FCSTD DOCUMENT  (FreeCAD 1.1R40971 (Git))
Label: neje-max-4
License: All rights reserved
LicenseURL: http://en.wikipedia.org/wiki/All_rights_reserved
objects: App::Link×5, App::DocumentObjectGroup×3, PartDesign::CoordinateSystem×1, App::FeaturePython×1, App::Part×1, App::Point×1
note: 1 computed .brp shape members not serialized (recipe doc carries the construction recipe); baked Part::Feature solids carry a one-line shape summary decoded from their .brp
EXTERNAL_REF file=x-frame.FCStd obj=Body
EXTERNAL_REF file=y-extrusion.FCStd obj=Body
EXTERNAL_REF file=x-rail-assy.FCStd obj=Part

FEATURE [App::DocumentObjectGroup] Parts
FEATURE [PartDesign::CoordinateSystem] LCS_Origin
  AttacherType = Attacher::AttachEngine3D
  AttachmentSupport = -> [X_Axis]
  MapMode = 2
FEATURE [App::DocumentObjectGroup] Constraints
FEATURE [App::FeaturePython] Variables  # WARN: FeaturePython — macro-defined, semantics opaque (R4)
  Type = App::PropertyContainer
FEATURE [App::DocumentObjectGroup] Configurations
FEATURE [App::Link] Body  label="rail-back"
  LinkPlacement = pos=(-2.5736e-05,294.386,0) rot=(0,0,1;3.14159rad)
  LinkedObject = -> <external x-frame.FCStd>#Body
  Placement = pos=(-2.5736e-05,294.386,0) rot=(0,0,1;3.14159rad)
FEATURE [App::Link] rail_back  label="rail-front"
  LinkPlacement = pos=(0,-294.386,0) rot=(0,0,1;0rad)
  LinkedObject = -> <external x-frame.FCStd>#Body
  Placement = pos=(0,-294.386,0) rot=(0,0,1;0rad)
FEATURE [App::Link] Body001  label="rail-left"
  LinkPlacement = pos=(-439.723,4.89331e-05,29.242) rot=(0,0,1;0rad)
  LinkedObject = -> <external y-extrusion.FCStd>#Body
  Placement = pos=(-439.723,4.89331e-05,29.242) rot=(0,0,1;0rad)
FEATURE [App::Link] Body002  label="rail-right"
  LinkPlacement = pos=(439.926,-5.59382e-05,29.3182) rot=(0,0,1;0rad)
  LinkedObject = -> <external y-extrusion.FCStd>#Body
  Placement = pos=(439.926,-5.59382e-05,29.3182) rot=(0,0,1;0rad)
FEATURE [App::Link] Part  label="x-rail"
  LinkPlacement = pos=(0,0,45.72) rot=(0,0,1;0rad)
  LinkedObject = -> <external x-rail-assy.FCStd>#Part
  Placement = pos=(0,0,45.72) rot=(0,0,1;0rad)
FEATURE [App::Part] Assembly
  AssemblyType = Part::Link
  Group = -> [LCS_Origin,Constraints,Variables,Configurations,Body,rail_back,Body001,Body002,Part]
  Origin = -> Origin
  Type = Assembly
FEATURE [App::Point] Origin001  label="Origin"
  Role = Origin

RESOLVED EXTERNAL PARTS (link-assembly join: the EXTERNAL_REF files above that resolve inside this repo's crawl, each included once):
---- part x-frame.FCStd = doc fcstd_80ce30af8bc4 ----
FCSTD DOCUMENT  (FreeCAD 1.1R40971 (Git))
Label: x-frame
License: All rights reserved
LicenseURL: http://en.wikipedia.org/wiki/All_rights_reserved
objects: Sketcher::SketchObject×4, PartDesign::Pocket×2, PartDesign::Pad×1, PartDesign::Hole×1, PartDesign::Body×1, App::Point×1
note: 21 computed .brp shape members not serialized (recipe doc carries the construction recipe); baked Part::Feature solids carry a one-line shape summary decoded from their .brp

FEATURE [Sketcher::SketchObject] Sketch
  ArcFitTolerance = 0
  ExternalTypes = [0]
  FullyConstrained = true
  MakeInternals = false
  Placement = pos=(0,0,0) rot=(0.57735,0.57735,0.57735;2.0944rad)
  sketch-geometry (6):
    g0: LineSegment StartX=0 StartY=60 StartZ=0 EndX=4.7 EndY=60 EndZ=0
    g1: LineSegment StartX=26 StartY=4.7 StartZ=0 EndX=26 EndY=0 EndZ=0
    g2: LineSegment StartX=26 StartY=0 StartZ=0 EndX=0 EndY=0 EndZ=0
    g3: LineSegment StartX=0 StartY=0 StartZ=0 EndX=0 EndY=60 EndZ=0
    g4: LineSegment StartX=26 StartY=4.7 StartZ=0 EndX=4.7 EndY=4.7 EndZ=0
    g5: LineSegment StartX=4.7 StartY=4.7 StartZ=0 EndX=4.7 EndY=60 EndZ=0
  constraints (17):
    c: Coincident(g1,g2)
    c: Coincident(g2,g3)
    c: Coincident(g3,g0)
    c: Horizontal(g0)
    c: Horizontal(g2)
    c: Vertical(g1)
    c: Vertical(g3)
    c: Coincident(g4,g5)
    c: Horizontal(g4)
    c: Vertical(g5)
    c: Coincident(g5,g0)
    c: Coincident(g4,g1)
    c: Equal(g1,g0)
    c: DistanceY(g1,g1) = 4.7
    c: DistanceX(g2,g2) = 26
    c: DistanceY(g3,g3) = 60
    c: Coincident(g2,g-1)
FEATURE [PartDesign::Pad] Pad
  Direction = (1,1e-16,-1e-16)
  Length = 920
  Length2 = 10
  Midplane = true
  Placement = pos=(0,0,0) rot=(0.57735,0.57735,0.57735;2.0944rad)
  Profile = -> Sketch
  ReferenceAxis = -> Sketch [N_Axis]
  Suppressed = false
  Type = 0
FEATURE [Sketcher::SketchObject] Sketch001
  ArcFitTolerance = 0
  AttachmentSupport = -> [Pad]
  ExternalTypes = [0]
  FullyConstrained = true
  MakeInternals = false
  MapMode = 5
  Placement = pos=(0,0,0) rot=(0.57735,0.57735,-0.57735;2.0944rad)
  sketch-geometry (8):
    g0: LineSegment StartX=-70 StartY=-427.5 StartZ=0 EndX=-36 EndY=-427.5 EndZ=0
    g1: LineSegment StartX=-30 StartY=-421.5 StartZ=0 EndX=-30 EndY=421.5 EndZ=0
    g2: LineSegment StartX=-36 StartY=427.5 StartZ=0 EndX=-70 EndY=427.5 EndZ=0
    g3: LineSegment StartX=-70 StartY=427.5 StartZ=0 EndX=-70 EndY=-427.5 EndZ=0
    g4: ArcOfCircle CenterX=-36 CenterY=-421.5 CenterZ=0 NormalX=0 NormalY=0 NormalZ=1 AngleXU=0 Radius=6 StartAngle=4.71239 EndAngle=6.28319
    g5: GeomPoint [constr] X=-30 Y=-427.5 Z=0
    g6: ArcOfCircle CenterX=-36 CenterY=421.5 CenterZ=0 NormalX=0 NormalY=0 NormalZ=1 AngleXU=0 Radius=6 StartAngle=-8.9e-13 EndAngle=1.5708
    g7: GeomPoint [constr] X=-30 Y=427.5 Z=0
  constraints (19):
    c: Coincident(g2,g3)
    c: Coincident(g3,g0)
    c: Horizontal(g0)
    c: Horizontal(g2)
    c: Vertical(g1)
    c: DistanceX(g7,g-1) = 30
    c: PointOnObject(g5,g0)
    c: PointOnObject(g5,g1)
    c: Tangent(g0,g4) = -1.5708
    c: Tangent(g1,g4) = -1.5708
    c: PointOnObject(g7,g1)
    c: PointOnObject(g7,g2)
    c: Tangent(g1,g6) = -1.5708
    c: Tangent(g2,g6) = -1.5708
    c: Equal(g6,g4)
    c: Diameter(g4) = 12
    c: DistanceX(g0,g-1) = 70
    c: Symmetric(g2,g0,g-1)
    c: DistanceY(g3,g3) = 855
FEATURE [PartDesign::Pocket] Pocket
  BaseFeature = -> Pad
  Direction = (0,1,0)
  Length = 5
  Length2 = 5
  Midplane = true
  Placement = pos=(0,0,0) rot=(0.57735,0.57735,0.57735;2.0944rad)
  Profile = -> Sketch001
  ReferenceAxis = -> Sketch001 [N_Axis]
  Suppressed = false
  Type = 1
FEATURE [Sketcher::SketchObject] Sketch002
  ArcFitTolerance = 0
  AttachmentSupport = -> [Pocket]
  ExternalTypes = [0]
  FullyConstrained = true
  MakeInternals = false
  MapMode = 5
  Placement = pos=(2.1e-15,-2.6e-15,4.7) rot=(0,0,-1;1.5708rad)
  sketch-geometry (41):
    g0: Circle CenterX=-14.7 CenterY=455 CenterZ=0 NormalX=0 NormalY=0 NormalZ=1 AngleXU=0 Radius=2.5
    g1: Circle CenterX=-14.7 CenterY=409.5 CenterZ=0 NormalX=0 NormalY=0 NormalZ=1 AngleXU=0 Radius=2.5
    g2: LineSegment [constr] StartX=-14.7 StartY=455 StartZ=0 EndX=-14.7 EndY=409.5 EndZ=0
    g3: Circle CenterX=-14.7 CenterY=364 CenterZ=0 NormalX=0 NormalY=0 NormalZ=1 AngleXU=0 Radius=2.5
    g4: LineSegment [constr] StartX=-14.7 StartY=409.5 StartZ=0 EndX=-14.7 EndY=364 EndZ=0
    g5: Circle CenterX=-14.7 CenterY=318.5 CenterZ=0 NormalX=0 NormalY=0 NormalZ=1 AngleXU=0 Radius=2.5
    g6: LineSegment [constr] StartX=-14.7 StartY=364 StartZ=0 EndX=-14.7 EndY=318.5 EndZ=0
    g7: Circle CenterX=-14.7 CenterY=273 CenterZ=0 NormalX=0 NormalY=0 NormalZ=1 AngleXU=0 Radius=2.5
    g8: LineSegment [constr] StartX=-14.7 StartY=318.5 StartZ=0 EndX=-14.7 EndY=273 EndZ=0
    g9: Circle CenterX=-14.7 CenterY=227.5 CenterZ=0 NormalX=0 NormalY=0 NormalZ=1 AngleXU=0 Radius=2.5
    g10: LineSegment [constr] StartX=-14.7 StartY=273 StartZ=0 EndX=-14.7 EndY=227.5 EndZ=0
    g11: Circle CenterX=-14.7 CenterY=182 CenterZ=0 NormalX=0 NormalY=0 NormalZ=1 AngleXU=0 Radius=2.5
    g12: LineSegment [constr] StartX=-14.7 StartY=227.5 StartZ=0 EndX=-14.7 EndY=182 EndZ=0
    g13: Circle CenterX=-14.7 CenterY=136.5 CenterZ=0 NormalX=0 NormalY=0 NormalZ=1 AngleXU=0 Radius=2.5
    g14: LineSegment [constr] StartX=-14.7 StartY=182 StartZ=0 EndX=-14.7 EndY=136.5 EndZ=0
    g15: Circle CenterX=-14.7 CenterY=91 CenterZ=0 NormalX=0 NormalY=0 NormalZ=1 AngleXU=0 Radius=2.5
    g16: LineSegment [constr] StartX=-14.7 StartY=136.5 StartZ=0 EndX=-14.7 EndY=91 EndZ=0
    g17: Circle CenterX=-14.7 CenterY=45.5 CenterZ=0 NormalX=0 NormalY=0 NormalZ=1 AngleXU=0 Radius=2.5
    g18: LineSegment [constr] StartX=-14.7 StartY=91 StartZ=0 EndX=-14.7 EndY=45.5 EndZ=0
    g19: Circle CenterX=-14.7 CenterY=0 CenterZ=0 NormalX=0 NormalY=0 NormalZ=1 AngleXU=0 Radius=2.5
    g20: LineSegment [constr] StartX=-14.7 StartY=45.5 StartZ=0 EndX=-14.7 EndY=0 EndZ=0
    g21: Circle CenterX=-14.7 CenterY=-45.5 CenterZ=0 NormalX=0 NormalY=0 NormalZ=1 AngleXU=0 Radius=2.5
    g22: LineSegment [constr] StartX=-14.7 StartY=0 StartZ=0 EndX=-14.7 EndY=-45.5 EndZ=0
    g23: Circle CenterX=-14.7 CenterY=-91 CenterZ=0 NormalX=0 NormalY=0 NormalZ=1 AngleXU=0 Radius=2.5
    g24: LineSegment [constr] StartX=-14.7 StartY=-45.5 StartZ=0 EndX=-14.7 EndY=-91 EndZ=0
    g25: Circle CenterX=-14.7 CenterY=-136.5 CenterZ=0 NormalX=0 NormalY=0 NormalZ=1 AngleXU=0 Radius=2.5
    g26: LineSegment [constr] StartX=-14.7 StartY=-91 StartZ=0 EndX=-14.7 EndY=-136.5 EndZ=0
    g27: Circle CenterX=-14.7 CenterY=-182 CenterZ=0 NormalX=0 NormalY=0 NormalZ=1 AngleXU=0 Radius=2.5
    g28: LineSegment [constr] StartX=-14.7 StartY=-136.5 StartZ=0 EndX=-14.7 EndY=-182 EndZ=0
    g29: Circle CenterX=-14.7 CenterY=-227.5 CenterZ=0 NormalX=0 NormalY=0 NormalZ=1 AngleXU=0 Radius=2.5
    g30: LineSegment [constr] StartX=-14.7 StartY=-182 StartZ=0 EndX=-14.7 EndY=-227.5 EndZ=0
    g31: Circle CenterX=-14.7 CenterY=-273 CenterZ=0 NormalX=0 NormalY=0 NormalZ=1 AngleXU=0 Radius=2.5
    g32: LineSegment [constr] StartX=-14.7 StartY=-227.5 StartZ=0 EndX=-14.7 EndY=-273 EndZ=0
    g33: Circle CenterX=-14.7 CenterY=-318.5 CenterZ=0 NormalX=0 NormalY=0 NormalZ=1 AngleXU=0 Radius=2.5
    g34: LineSegment [constr] StartX=-14.7 StartY=-273 StartZ=0 EndX=-14.7 EndY=-318.5 EndZ=0
    g35: Circle CenterX=-14.7 CenterY=-364 CenterZ=0 NormalX=0 NormalY=0 NormalZ=1 AngleXU=0 Radius=2.5
    g36: LineSegment [constr] StartX=-14.7 StartY=-318.5 StartZ=0 EndX=-14.7 EndY=-364 EndZ=0
    g37: Circle CenterX=-14.7 CenterY=-409.5 CenterZ=0 NormalX=0 NormalY=0 NormalZ=1 AngleXU=0 Radius=2.5
    g38: LineSegment [constr] StartX=-14.7 StartY=-364 StartZ=0 EndX=-14.7 EndY=-409.5 EndZ=0
    g39: Circle CenterX=-14.7 CenterY=-455 CenterZ=0 NormalX=0 NormalY=0 NormalZ=1 AngleXU=0 Radius=2.5
    g40: LineSegment [constr] StartX=-14.7 StartY=-409.5 StartZ=0 EndX=-14.7 EndY=-455 EndZ=0
  constraints (102):
    c: Diameter(g0) = 5
    c: Equal(g0,g1) = 5
    c: Coincident(g0,g2)
    c: Coincident(g1,g2)
    c: Distance(g2) = 45.5
    c: Equal(g0,g3) = 5
    c: Coincident(g1,g4)
    c: Coincident(g3,g4)
    c: Equal(g2,g4)
    c: Parallel(g4,g2)
    c: Equal(g0,g5) = 5
    c: Coincident(g3,g6)
    c: Coincident(g5,g6)
    c: Equal(g2,g6)
    c: Parallel(g6,g2)
    c: Equal(g0,g7) = 5
    c: Coincident(g5,g8)
    c: Coincident(g7,g8)
    c: Equal(g2,g8)
    c: Parallel(g8,g2)
    c: Equal(g0,g9) = 5
    c: Coincident(g7,g10)
    c: Coincident(g9,g10)
    c: Equal(g2,g10)
    c: Parallel(g10,g2)
    c: Equal(g0,g11) = 5
    c: Coincident(g9,g12)
    c: Coincident(g11,g12)
    c: Equal(g2,g12)
    c: Parallel(g12,g2)
    c: Equal(g0,g13) = 5
    c: Coincident(g11,g14)
    c: Coincident(g13,g14)
    c: Equal(g2,g14)
    c: Parallel(g14,g2)
    c: Equal(g0,g15) = 5
    c: Coincident(g13,g16)
    c: Coincident(g15,g16)
    c: Equal(g2,g16)
    c: Parallel(g16,g2)
    c: Equal(g0,g17) = 5
    c: Coincident(g15,g18)
    c: Coincident(g17,g18)
    c: Equal(g2,g18)
    c: Parallel(g18,g2)
    c: Equal(g0,g19) = 5
    c: Coincident(g17,g20)
    c: Coincident(g19,g20)
    c: Equal(g2,g20)
    c: Parallel(g20,g2)
    c: Equal(g0,g21) = 5
    c: Coincident(g19,g22)
    c: Coincident(g21,g22)
    c: Equal(g2,g22)
    c: Parallel(g22,g2)
    c: Equal(g0,g23) = 5
    c: Coincident(g21,g24)
    c: Coincident(g23,g24)
    c: Equal(g2,g24)
    c: Parallel(g24,g2)
    c: Equal(g0,g25) = 5
    c: Coincident(g23,g26)
    c: Coincident(g25,g26)
    c: Equal(g2,g26)
    c: Parallel(g26,g2)
    c: Equal(g0,g27) = 5
    c: Coincident(g25,g28)
    c: Coincident(g27,g28)
    c: Equal(g2,g28)
    c: Parallel(g28,g2)
    c: Equal(g0,g29) = 5
    c: Coincident(g27,g30)
    c: Coincident(g29,g30)
    c: Equal(g2,g30)
    c: Parallel(g30,g2)
    c: Equal(g0,g31) = 5
    c: Coincident(g29,g32)
    c: Coincident(g31,g32)
    c: Equal(g2,g32)
    c: Parallel(g32,g2)
    c: Equal(g0,g33) = 5
    c: Coincident(g31,g34)
    c: Coincident(g33,g34)
    c: Equal(g2,g34)
    c: Parallel(g34,g2)
    c: Equal(g0,g35) = 5
    c: Coincident(g33,g36)
    c: Coincident(g35,g36)
    c: Equal(g2,g36)
    c: Parallel(g36,g2)
    c: Equal(g0,g37) = 5
    c: Coincident(g35,g38)
    c: Coincident(g37,g38)
    c: Equal(g2,g38)
    c: Parallel(g38,g2)
    c: Equal(g0,g39) = 5
    c: Coincident(g37,g40)
    c: Coincident(g39,g40)
    c: Equal(g2,g40)
    c: Parallel(g40,g2)
    c: DistanceX(g39,g-1) = 14.7
    c: Symmetric(g39,g0,g-1)
FEATURE [PartDesign::Hole] Hole
  BaseFeature = -> Pocket
  CustomThreadClearance = 0
  Depth = 25
  DepthType = 0
  Diameter = 6
  DrillForDepth = false
  DrillPoint = 1
  DrillPointAngle = 118
  HoleCutCountersinkAngle = 90
  HoleCutCustomValues = false
  HoleCutDepth = 0
  HoleCutDiameter = 6.1
  HoleCutType = 0
  ModelThread = false
  Placement = pos=(0,0,0) rot=(0.57735,0.57735,0.57735;2.0944rad)
  Profile = -> Sketch002
  Suppressed = false
  Tapered = false
  TaperedAngle = 90
  ThreadClass = 0
  ThreadDepth = 25
  ThreadDepthType = 0
  ThreadDiameter = 6
  ThreadDirection = 0
  ThreadFit = 0
  ThreadSize = 0
  ThreadType = 0
  Threaded = false
  UseCustomThreadClearance = false
FEATURE [Sketcher::SketchObject] Sketch003
  ArcFitTolerance = 0
  AttachmentSupport = -> [Hole]
  ExternalTypes = [0]
  FullyConstrained = true
  MakeInternals = false
  MapMode = 5
  Placement = pos=(-5.7e-15,4.7,3.7e-15) rot=(-0.57735,-0.57735,-0.57735;2.0944rad)
  sketch-geometry (18):
    g0: Circle CenterX=37.3 CenterY=-440 CenterZ=0 NormalX=0 NormalY=0 NormalZ=1 AngleXU=0 Radius=3.25
    g1: Circle CenterX=51.3 CenterY=-440 CenterZ=0 NormalX=0 NormalY=0 NormalZ=1 AngleXU=0 Radius=3.25
    g2: ArcOfCircle CenterX=56 CenterY=-437.75 CenterZ=0 NormalX=0 NormalY=0 NormalZ=1 AngleXU=0 Radius=1 StartAngle=2.4027e-12 EndAngle=3.14159
    g3: ArcOfCircle CenterX=56 CenterY=-442.25 CenterZ=0 NormalX=0 NormalY=0 NormalZ=1 AngleXU=0 Radius=1 StartAngle=3.14159 EndAngle=6.28319
    g4: LineSegment StartX=57 StartY=-437.75 StartZ=0 EndX=57 EndY=-442.25 EndZ=0
    g5: LineSegment StartX=55 StartY=-437.75 StartZ=0 EndX=55 EndY=-442.25 EndZ=0
    g6: Circle CenterX=37.3 CenterY=440 CenterZ=0 NormalX=0 NormalY=0 NormalZ=1 AngleXU=0 Radius=3.25
    g7: Circle CenterX=51.3 CenterY=440 CenterZ=0 NormalX=0 NormalY=0 NormalZ=1 AngleXU=0 Radius=3.25
    g8: LineSegment StartX=57 StartY=437.75 StartZ=0 EndX=57 EndY=442.25 EndZ=0
    g9: LineSegment StartX=59 StartY=442.25 StartZ=0 EndX=59 EndY=437.75 EndZ=0
    g10: ArcOfCircle CenterX=58 CenterY=437.75 CenterZ=0 NormalX=0 NormalY=0 NormalZ=1 AngleXU=0 Radius=1 StartAngle=3.14159 EndAngle=6.28319
    g11: ArcOfCircle CenterX=58 CenterY=442.25 CenterZ=0 NormalX=0 NormalY=0 NormalZ=1 AngleXU=0 Radius=1 StartAngle=5.7e-15 EndAngle=3.14159
    g12: LineSegment [constr] StartX=37.3 StartY=-440 StartZ=0 EndX=51.3 EndY=-440 EndZ=0
    g13: LineSegment [constr] StartX=51.3 StartY=-440 StartZ=0 EndX=57 EndY=-440 EndZ=0
    g14: LineSegment [constr] StartX=37.3 StartY=440 StartZ=0 EndX=51.3 EndY=440 EndZ=0
    g15: LineSegment [constr] StartX=51.3 StartY=440 StartZ=0 EndX=57 EndY=440 EndZ=0
    g16: GeomPoint [constr] X=51.3 Y=-443.25 Z=0
    g17: GeomPoint [constr] X=56 Y=-443.25 Z=0
  constraints (43):
    c: Equal(g0,g1)
    c: Diameter(g1) = 6.5
    c: Horizontal(g0,g1)
    c: DistanceX(g0,g1) = 14
    c: Parallel(g5,g4)
    c: Tangent(g2,g4) = 1.5708
    c: Tangent(g3,g5) = -1.5708
    c: Diameter(g2) = 2
    c: Vertical(g2,g3)
    c: Tangent(g2,g5) = -1.5708
    c: Tangent(g3,g4) = 1.5708
    c: DistanceX(g1,g2) = 3.7
    c: Vertical(g8)
    c: Vertical(g9)
    c: Equal(g0,g6)
    c: Equal(g6,g7)
    c: Horizontal(g6,g7)
    c: Tangent(g10,g9) = 1.5708
    c: Tangent(g10,g8) = 1.5708
    c: Tangent(g11,g8) = 1.5708
    c: Tangent(g11,g9) = 1.5708
    c: Equal(g2,g11)
    c: Equal(g8,g4)
    c: Coincident(g12,g0)
    c: Coincident(g12,g1)
    c: Coincident(g13,g1)
    c: Horizontal(g13)
    c: Symmetric(g2,g3,g13)
    c: Coincident(g14,g6)
    c: Coincident(g14,g7)
    c: Coincident(g15,g7)
    c: Horizontal(g15)
    c: Symmetric(g8,g8,g15)
    c: Equal(g15,g13)
    c: Equal(g12,g14)
    c: Symmetric(g6,g0,g-1)
    c: DistanceY(g0,g6) = 880
    c: PointOnObject(g16,g1)
    c: PointOnObject(g17,g3)
    c: Vertical(g17,g3)
    c: Vertical(g16,g1)
    c: Horizontal(g16,g17)
    c: DistanceX(g-1,g2) = 57
FEATURE [PartDesign::Pocket] Pocket001
  BaseFeature = -> Hole
  Direction = (1e-15,-1,1e-16)
  Length = 5
  Length2 = 5
  Placement = pos=(0,0,0) rot=(0.57735,0.57735,0.57735;2.0944rad)
  Profile = -> Sketch003
  ReferenceAxis = -> Sketch003 [N_Axis]
  Suppressed = false
  Type = 1
FEATURE [PartDesign::Body] Body
  AllowCompound = false
  Group = -> [Sketch,Pad,Sketch001,Pocket,Sketch002,Hole,Sketch003,Pocket001]
  Origin = -> Origin
  Tip = -> Pocket001
FEATURE [App::Point] Origin001  label="Origin"
  Role = Origin
---- part x-rail-assy.FCStd = doc fcstd_7c6b1dbbf69c ----
FCSTD DOCUMENT  (FreeCAD 1.1R40971 (Git))
Label: x-rail-assy
License: All rights reserved
LicenseURL: http://en.wikipedia.org/wiki/All_rights_reserved
objects: App::Link×3, App::Part×1, App::Point×1
EXTERNAL_REF file=nema-17.FCStd obj=Body
EXTERNAL_REF file=x-rail.FCStd obj=Body

FEATURE [App::Link] Body_1  label="motor-y0"
  LinkPlacement = pos=(-495.808,-3.94195,45.426) rot=(0,0,1;0rad)
  LinkedObject = -> <external nema-17.FCStd>#Body
  Placement = pos=(-495.808,-3.94195,45.426) rot=(0,0,1;0rad)
FEATURE [App::Link] Body  label="rail"
  LinkedObject = -> <external x-rail.FCStd>#Body
FEATURE [App::Link] Body002  label="motor-x"
  LinkPlacement = pos=(403.97,18.27,-9.11998) rot=(0.57735,0.57735,0.57735;2.0944rad)
  LinkedObject = -> <external nema-17.FCStd>#Body
  Placement = pos=(403.97,18.27,-9.11998) rot=(0.57735,0.57735,0.57735;2.0944rad)
FEATURE [App::Part] Part
  Group = -> [Body_1,Body,Body002]
  Origin = -> Origin
FEATURE [App::Point] Origin001  label="Origin"
  Role = Origin
---- part y-extrusion.FCStd = doc fcstd_32d3a53af580 ----
FCSTD DOCUMENT  (FreeCAD 1.1R40971 (Git))
Label: y-extrusion
License: All rights reserved
LicenseURL: http://en.wikipedia.org/wiki/All_rights_reserved
objects: Sketcher::SketchObject×1, PartDesign::Pad×1, PartDesign::Body×1, App::Point×1
note: 6 computed .brp shape members not serialized (recipe doc carries the construction recipe); baked Part::Feature solids carry a one-line shape summary decoded from their .brp

FEATURE [Sketcher::SketchObject] Sketch
  ArcFitTolerance = 0
  AttachmentSupport = -> [XZ_Plane]
  ExternalTypes = [0]
  FullyConstrained = false
  MakeInternals = false
  MapMode = 5
  Placement = pos=(0,0,0) rot=(1,0,0;1.5708rad)
  sketch-geometry (75):
    g0: LineSegment StartX=-10 StartY=30 StartZ=0 EndX=-3 EndY=30 EndZ=0
    g1: LineSegment StartX=10 StartY=30 StartZ=0 EndX=10 EndY=25 EndZ=0
    g2: LineSegment StartX=10 StartY=0 StartZ=0 EndX=3 EndY=0 EndZ=0
    g3: LineSegment StartX=-10 StartY=0 StartZ=0 EndX=-10 EndY=5 EndZ=0
    g4: LineSegment StartX=-3 StartY=0 StartZ=0 EndX=-3 EndY=1.5 EndZ=0
    g5: LineSegment StartX=-3 StartY=1.5 StartZ=0 EndX=-4.5 EndY=1.5 EndZ=0
    g6: LineSegment StartX=-4.5 StartY=1.5 StartZ=0 EndX=-4.5 EndY=3 EndZ=0
    g7: LineSegment StartX=-4.5 StartY=3 StartZ=0 EndX=-1.5 EndY=6 EndZ=0
    g8: LineSegment StartX=-1.5 StartY=6 StartZ=0 EndX=1.5 EndY=6 EndZ=0
    g9: LineSegment StartX=1.5 StartY=6 StartZ=0 EndX=4.5 EndY=3 EndZ=0
    g10: LineSegment StartX=4.5 StartY=3 StartZ=0 EndX=4.5 EndY=1.5 EndZ=0
    g11: LineSegment StartX=4.5 StartY=1.5 StartZ=0 EndX=3 EndY=1.5 EndZ=0
    g12: LineSegment StartX=3 StartY=1.5 StartZ=0 EndX=3 EndY=0 EndZ=0
    g13: LineSegment StartX=-3 StartY=0 StartZ=0 EndX=-10 EndY=0 EndZ=0
    g14: LineSegment StartX=-10 StartY=5 StartZ=0 EndX=-8.5 EndY=5 EndZ=0
    g15: LineSegment StartX=-8.5 StartY=5 StartZ=0 EndX=-8.5 EndY=3.5 EndZ=0
    g16: LineSegment StartX=-8.5 StartY=3.5 StartZ=0 EndX=-7 EndY=3.5 EndZ=0
    g17: LineSegment StartX=-7 StartY=3.5 StartZ=0 EndX=-4 EndY=6.5 EndZ=0
    g18: LineSegment StartX=-4 StartY=6.5 StartZ=0 EndX=-4 EndY=9.5 EndZ=0
    g19: LineSegment StartX=-4 StartY=9.5 StartZ=0 EndX=-7 EndY=12.5 EndZ=0
    g20: LineSegment StartX=-7 StartY=12.5 StartZ=0 EndX=-8.5 EndY=12.5 EndZ=0
    g21: LineSegment StartX=-8.5 StartY=12.5 StartZ=0 EndX=-8.5 EndY=11 EndZ=0
    g22: LineSegment StartX=-8.5 StartY=11 StartZ=0 EndX=-10 EndY=11 EndZ=0
    g23: LineSegment [constr] StartX=-9.99569 StartY=8 StartZ=0 EndX=10 EndY=8 EndZ=0
    g24: LineSegment StartX=-10 StartY=11 StartZ=0 EndX=-10 EndY=19 EndZ=0
    g25: LineSegment StartX=-10 StartY=25 StartZ=0 EndX=-8.5 EndY=25 EndZ=0
    g26: LineSegment StartX=-8.5 StartY=25 StartZ=0 EndX=-8.5 EndY=26.5 EndZ=0
    g27: LineSegment StartX=-8.5 StartY=26.5 StartZ=0 EndX=-7 EndY=26.5 EndZ=0
    g28: LineSegment StartX=-7 StartY=26.5 StartZ=0 EndX=-4 EndY=23.5 EndZ=0
    g29: LineSegment StartX=-4 StartY=23.5 StartZ=0 EndX=-4 EndY=20.5 EndZ=0
    g30: LineSegment StartX=-4 StartY=20.5 StartZ=0 EndX=-7 EndY=17.5 EndZ=0
    g31: LineSegment StartX=-7 StartY=17.5 StartZ=0 EndX=-8.5 EndY=17.5 EndZ=0
    g32: LineSegment StartX=-8.5 StartY=17.5 StartZ=0 EndX=-8.5 EndY=19 EndZ=0
    g33: LineSegment StartX=-8.5 StartY=19 StartZ=0 EndX=-10 EndY=19 EndZ=0
    g34: LineSegment [constr] StartX=-10 StartY=22 StartZ=0 EndX=9.99999 EndY=22 EndZ=0
    g35: LineSegment StartX=-10 StartY=25 StartZ=0 EndX=-10 EndY=30 EndZ=0
    g36: LineSegment StartX=-3 StartY=30 StartZ=0 EndX=-3 EndY=28.5 EndZ=0
    g37: LineSegment StartX=-3 StartY=28.5 StartZ=0 EndX=-4.5 EndY=28.5 EndZ=0
    g38: LineSegment StartX=-4.5 StartY=28.5 StartZ=0 EndX=-4.5 EndY=27 EndZ=0
    g39: LineSegment StartX=-4.5 StartY=27 StartZ=0 EndX=-1.5 EndY=24 EndZ=0
    g40: LineSegment StartX=-1.5 StartY=24 StartZ=0 EndX=1.5 EndY=24 EndZ=0
    g41: LineSegment StartX=1.5 StartY=24 StartZ=0 EndX=4.5 EndY=27 EndZ=0
    g42: LineSegment StartX=4.5 StartY=27 StartZ=0 EndX=4.5 EndY=28.5 EndZ=0
    g43: LineSegment StartX=4.5 StartY=28.5 StartZ=0 EndX=3 EndY=28.5 EndZ=0
    g44: LineSegment StartX=3 StartY=28.5 StartZ=0 EndX=3 EndY=30 EndZ=0
    g45: LineSegment StartX=3 StartY=30 StartZ=0 EndX=10 EndY=30 EndZ=0
    g46: LineSegment StartX=10 StartY=25 StartZ=0 EndX=8.5 EndY=25 EndZ=0
    g47: LineSegment StartX=8.5 StartY=25 StartZ=0 EndX=8.5 EndY=26.5 EndZ=0
    g48: LineSegment StartX=8.5 StartY=26.5 StartZ=0 EndX=7 EndY=26.5 EndZ=0
    g49: LineSegment StartX=7 StartY=26.5 StartZ=0 EndX=4 EndY=23.5 EndZ=0
    g50: LineSegment StartX=4 StartY=23.5 StartZ=0 EndX=4 EndY=20.5 EndZ=0
    g51: LineSegment StartX=4 StartY=20.5 StartZ=0 EndX=7 EndY=17.5 EndZ=0
    g52: LineSegment StartX=7 StartY=17.5 StartZ=0 EndX=8.5 EndY=17.5 EndZ=0
    g53: LineSegment StartX=8.5 StartY=17.5 StartZ=0 EndX=8.5 EndY=19 EndZ=0
    g54: LineSegment StartX=8.5 StartY=19 StartZ=0 EndX=10 EndY=19 EndZ=0
    g55: LineSegment StartX=10 StartY=19 StartZ=0 EndX=10 EndY=11 EndZ=0
    g56: LineSegment StartX=10 StartY=11 StartZ=0 EndX=8.5 EndY=11 EndZ=0
    g57: LineSegment StartX=8.5 StartY=11 StartZ=0 EndX=8.5 EndY=12.5 EndZ=0
    g58: LineSegment StartX=8.5 StartY=12.5 StartZ=0 EndX=7 EndY=12.5 EndZ=0
    g59: LineSegment StartX=7 StartY=12.5 StartZ=0 EndX=4 EndY=9.5 EndZ=0
    g60: LineSegment StartX=4 StartY=9.5 StartZ=0 EndX=4 EndY=6.5 EndZ=0
    g61: LineSegment StartX=4 StartY=6.5 StartZ=0 EndX=7 EndY=3.5 EndZ=0
    g62: LineSegment StartX=7 StartY=3.5 StartZ=0 EndX=8.5 EndY=3.5 EndZ=0
    g63: LineSegment StartX=8.5 StartY=3.5 StartZ=0 EndX=8.5 EndY=5 EndZ=0
    g64: LineSegment StartX=8.5 StartY=5 StartZ=0 EndX=10 EndY=5 EndZ=0
    g65: LineSegment StartX=10 StartY=5 StartZ=0 EndX=10 EndY=0 EndZ=0
    g66: Circle CenterX=0 CenterY=8 CenterZ=0 NormalX=0 NormalY=0 NormalZ=1 AngleXU=0 Radius=1.5
    g67: Circle CenterX=0 CenterY=22 CenterZ=0 NormalX=0 NormalY=0 NormalZ=1 AngleXU=0 Radius=1.5
    g68: LineSegment StartX=-7 StartY=15 StartZ=0 EndX=-2.71635 EndY=19.2836 EndZ=0
    g69: LineSegment StartX=-2.71635 StartY=19.2836 StartZ=0 EndX=2.71635 EndY=19.2836 EndZ=0
    g70: LineSegment StartX=2.71635 StartY=19.2836 StartZ=0 EndX=7 EndY=15 EndZ=0
    g71: LineSegment StartX=7 StartY=15 StartZ=0 EndX=2.71635 EndY=10.7164 EndZ=0
    g72: LineSegment StartX=2.71635 StartY=10.7164 StartZ=0 EndX=-2.71635 EndY=10.7164 EndZ=0
    g73: LineSegment StartX=-2.71635 StartY=10.7164 StartZ=0 EndX=-7 EndY=15 EndZ=0
    g74: LineSegment [constr] StartX=-10 StartY=15 StartZ=0 EndX=10 EndY=15 EndZ=0
  constraints (212):
    c: Coincident(g45,g1)
    c: Coincident(g65,g2)
    c: Coincident(g13,g3)
    c: Coincident(g35,g0)
    c: Horizontal(g0)
    c: Horizontal(g2)
    c: Vertical(g1)
    c: Vertical(g3)
    c: Symmetric(g65,g13,g-1)
    c: DistanceX(g13,g2) = 20
    c: DistanceY(g3,g35) = 30
    c: Vertical(g4)
    c: Coincident(g4,g5)
    c: Horizontal(g5)
    c: Coincident(g5,g6)
    c: Vertical(g6)
    c: Coincident(g6,g7)
    c: Coincident(g7,g8)
    c: Coincident(g8,g9)
    c: Coincident(g9,g10)
    c: Vertical(g10)
    c: Coincident(g10,g11)
    c: Horizontal(g11)
    c: Coincident(g11,g12)
    c: Vertical(g12)
    c: Equal(g6,g5)
    c: Equal(g5,g4)
    c: Equal(g4,g12)
    c: Equal(g12,g11)
    c: Equal(g11,g10)
    c: Distance(g4) = 1.5
    c: DistanceX(g4,g12) = 6
    c: Symmetric(g12,g4,g-2)
    c: Perpendicular(g9,g7)
    c: Symmetric(g7,g8,g-2)
    c: DistanceY(g4,g7) = 6
    c: Coincident(g13,g4)
    c: PointOnObject(g4,g-1)
    c: Coincident(g12,g2)
    c: Coincident(g14,g15)
    c: Coincident(g15,g16)
    c: Horizontal(g16)
    c: Coincident(g16,g17)
    c: Coincident(g17,g18)
    c: Vertical(g18)
    c: Coincident(g18,g19)
    c: Coincident(g19,g20)
    c: Coincident(g20,g21)
    c: Vertical(g21)
    c: Coincident(g21,g22)
    c: Horizontal(g22)
    c: Horizontal(g20)
    c: Vertical(g15)
    c: Equal(g6,g16)
    c: Equal(g16,g15)
    c: Equal(g15,g14)
    c: Equal(g14,g22)
    c: Equal(g22,g21)
    c: Equal(g21,g20)
    c: Perpendicular(g17,g19)
    c: PointOnObject(g23,g1)
    c: Symmetric(g22,g14,g23)
    c: Horizontal(g14)
    c: Symmetric(g17,g18,g23)
    c: Equal(g19,g7)
    c: Equal(g8,g18)
    c: Coincident(g3,g14)
    c: DistanceY(g3,g3) = 5
    c: Horizontal(g25)
    c: Coincident(g25,g26)
    c: Vertical(g26)
    c: Coincident(g26,g27)
    c: Coincident(g27,g28)
    c: Coincident(g28,g29)
    c: Vertical(g29)
    c: Coincident(g29,g30)
    c: Coincident(g30,g31)
    c: Horizontal(g31)
    c: Coincident(g31,g32)
    c: Coincident(g32,g33)
    c: Horizontal(g33)
    c: Symmetric(g29,g28,g34)
    c: Symmetric(g25,g33,g34)
    c: Vertical(g32)
    c: Horizontal(g27)
    c: Equal(g6,g31)
    c: Equal(g31,g32)
    c: Equal(g32,g33)
    c: Equal(g33,g25)
    c: Equal(g25,g26)
    c: Equal(g26,g27)
    c: Equal(g8,g29)
    c: Equal(g30,g7)
    c: Coincident(g35,g25)
    c: Coincident(g24,g33)
    c: Equal(g35,g3)
    c: Vertical(g24)
    c: Vertical(g35)
    c: Coincident(g22,g24)
    c: Perpendicular(g30,g28)
    c: Vertical(g36)
    c: Coincident(g36,g37)
    c: Horizontal(g37)
    c: Coincident(g37,g38)
    c: Vertical(g38)
    c: Coincident(g38,g39)
    c: Coincident(g39,g40)
    c: Horizontal(g40)
    c: Coincident(g40,g41)
    c: Coincident(g41,g42)
    c: Vertical(g42)
    c: Coincident(g42,g43)
    c: Horizontal(g43)
    c: Coincident(g43,g44)
    c: Vertical(g44)
    c: Coincident(g0,g36)
    c: Coincident(g45,g44)
    c: Symmetric(g0,g44,g-2)
    c: Equal(g38,g37)
    c: Equal(g37,g36)
    c: Equal(g36,g44)
    c: Equal(g44,g43)
    c: Equal(g43,g42)
    c: Equal(g0,g45)
    c: Equal(g39,g41)
    c: Equal(g41,g7)
    c: Perpendicular(g41,g39)
    c: Equal(g38,g6)
    c: Equal(g40,g8)
    c: Horizontal(g46)
    c: Coincident(g46,g47)
    c: Vertical(g47)
    c: Coincident(g47,g48)
    c: Horizontal(g48)
    c: Coincident(g48,g49)
    c: Coincident(g49,g50)
    c: Coincident(g50,g51)
    c: Coincident(g51,g52)
    c: Horizontal(g52)
    c: Coincident(g52,g53)
    c: Vertical(g53)
    c: Coincident(g53,g54)
    c: PointOnObject(g54,g1)
    c: Horizontal(g54)
    c: Symmetric(g49,g50,g34)
    c: Perpendicular(g51,g49)
    c: Equal(g48,g47)
    c: Equal(g47,g46)
    c: Equal(g46,g54)
    c: Equal(g54,g53)
    c: Equal(g53,g52)
    c: Equal(g52,g6)
    c: Equal(g49,g51)
    c: Equal(g8,g50)
    c: Coincident(g1,g46)
    c: PointOnObject(g55,g54)
    c: Equal(g51,g7)
    c: Equal(g1,g35)
    c: Horizontal(g56)
    c: Coincident(g56,g57)
    c: Vertical(g57)
    c: Coincident(g57,g58)
    c: Horizontal(g58)
    c: Coincident(g58,g59)
    c: Coincident(g59,g60)
    c: Coincident(g60,g61)
    c: Coincident(g61,g62)
    c: Horizontal(g62)
    c: Coincident(g62,g63)
    c: Vertical(g63)
    c: Coincident(g63,g64)
    c: Horizontal(g64)
    c: Coincident(g65,g64)
    c: Coincident(g55,g56)
    c: Symmetric(g55,g64,g23)
    c: Symmetric(g59,g60,g23)
    c: Equal(g58,g57)
    c: Equal(g57,g56)
    c: Equal(g56,g64)
    c: Equal(g64,g63)
    c: Equal(g63,g62)
    c: Equal(g62,g6)
    c: Equal(g8,g60)
    c: Vertical(g55)
    c: Vertical(g65)
    c: Equal(g65,g1)
    c: Equal(g61,g7)
    c: PointOnObject(g67,g-2)
    c: PointOnObject(g34,g3)
    c: Diameter(g66) = 3
    c: Coincident(g68,g69)
    c: Horizontal(g69)
    c: Coincident(g69,g70)
    c: Coincident(g70,g71)
    c: Coincident(g71,g72)
    c: Coincident(g72,g73)
    c: Coincident(g73,g68)
    c: Perpendicular(g73,g68)
    c: Perpendicular(g71,g70)
    c: Parallel(g59,g71)
    c: Parallel(g73,g19)
    c: Symmetric(g71,g72,g-2)
    c: Equal(g71,g73)
    c: PointOnObject(g74,g24)
    c: PointOnObject(g74,g55)
    c: Symmetric(g0,g3,g74)
    c: PointOnObject(g70,g74)
    c: Equal(g66,g67)
    c: Symmetric(g67,g66,g74)
    c: Equal(g72,g69)
    c: Vertical(g30,g68)
    c: DistanceY(g66,g67) = 14
FEATURE [PartDesign::Pad] Pad
  Direction = (0,-1,2e-16)
  Length = 580
  Length2 = 10
  Midplane = true
  Placement = pos=(0,0,0) rot=(1,0,0;1.5708rad)
  Profile = -> Sketch
  ReferenceAxis = -> Sketch [N_Axis]
  Suppressed = false
  Type = 0
FEATURE [PartDesign::Body] Body
  AllowCompound = false
  Group = -> [Sketch,Pad]
  Origin = -> Origin
  Tip = -> Pad
FEATURE [App::Point] Origin001  label="Origin"
  Role = Origin
